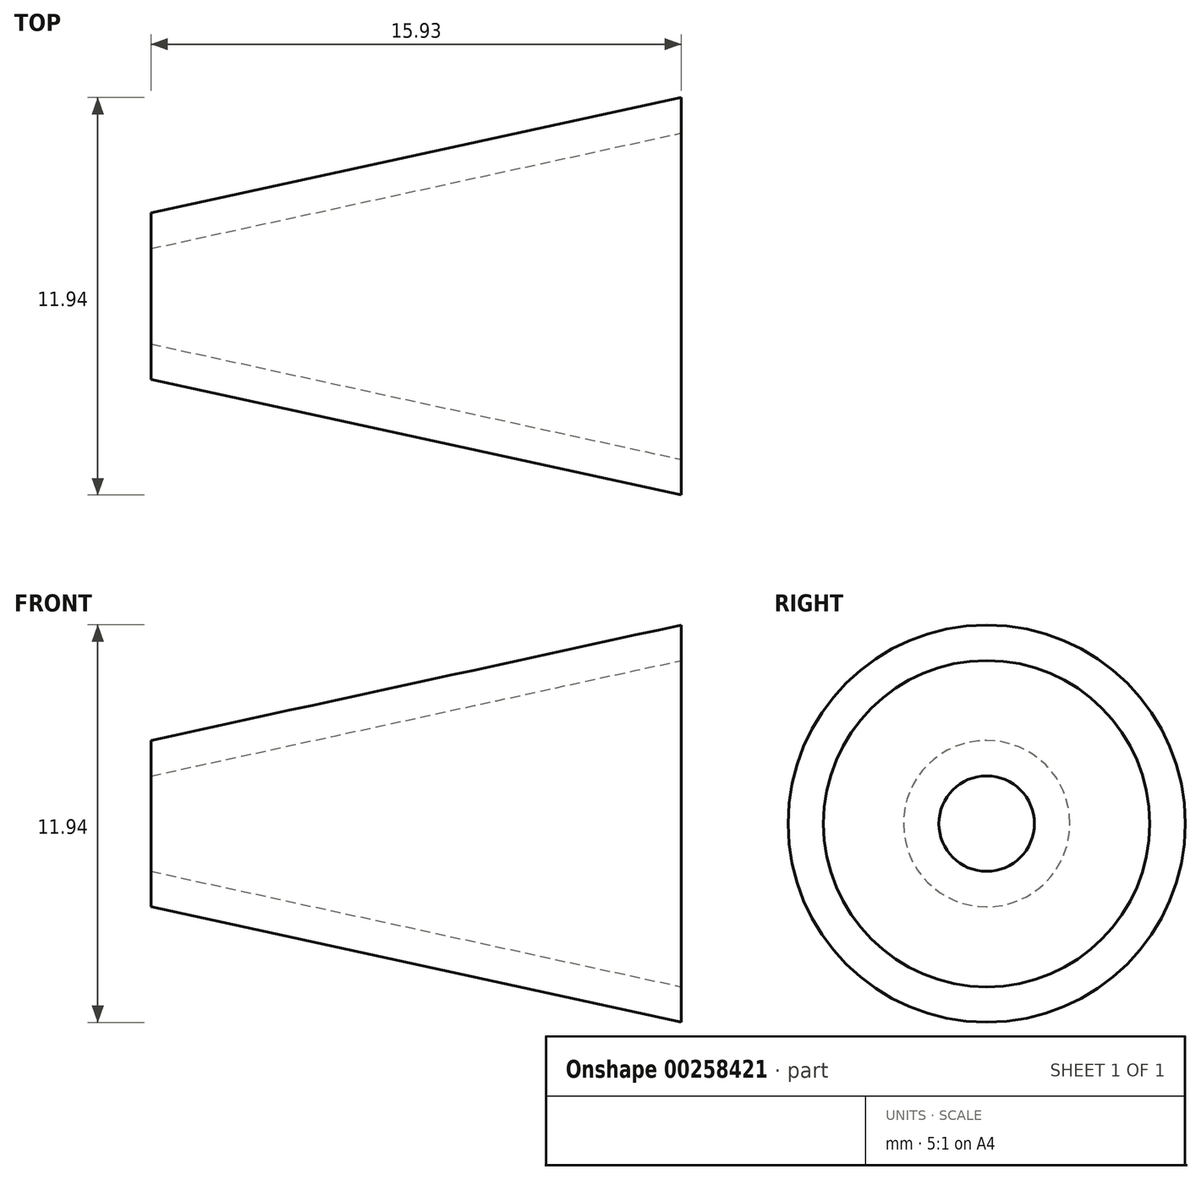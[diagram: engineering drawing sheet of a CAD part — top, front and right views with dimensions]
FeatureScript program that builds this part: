
annotation { "Feature Type Name" : "Feature", "Feature Type Description" : "" }
export const myFeature = defineFeature(function(context is Context, id is Id, definition is map)
    precondition{}
    {
        {
            var Q0;
            Q0=qCreatedBy(makeId("Front.planeOp"),FACE);
            var sketch = newSketch(context, id + "F0", { "sketchPlane" : qUnion([Q0])});
            skLineSegment(sketch, "E0", {"start": v(-15.93, 0) * mm, "end": v(-15.93, 2.5) * mm, "construction": true});
            skLineSegment(sketch, "E1.MirrorCS", {"start": v(-15.93, 0) * mm, "end": v(-15.93, -2.5) * mm, "construction": true});
            skLineSegment(sketch, "E2", {"start": v(-15.93, 2.5) * mm, "end": v(0, 5.97) * mm});
            skLineSegment(sketch, "E3", {"start": v(0, 5.97) * mm, "end": v(0, 4.9) * mm});
            skLineSegment(sketch, "E4", {"start": v(0, 4.9) * mm, "end": v(-15.93, 1.43) * mm});
            skLineSegment(sketch, "E5", {"start": v(-15.93, 1.43) * mm, "end": v(-15.93, 2.5) * mm});
            skLineSegment(sketch, "E6", {"start": v(-18.16, 0) * mm, "end": v(9.88, 0) * mm, "construction": true});
            skLineSegment(sketch, "E7", {"start": v(0, 4.9) * mm, "end": v(0, 0) * mm, "construction": true});
            skSolve(sketch);
        }
        {
            var Q0;
            Q0 = qSketchRegion(id + "F0", true);
            var Q1;
            Q1=sQuery(id+"F0.wireOp",EDGE,"E6");
            revolve(context, id + "F1", {"entities" : qUnion([Q0]), "axis" : qUnion([Q1]), "revolveType" : RevolveType.FULL});
        }
    });
